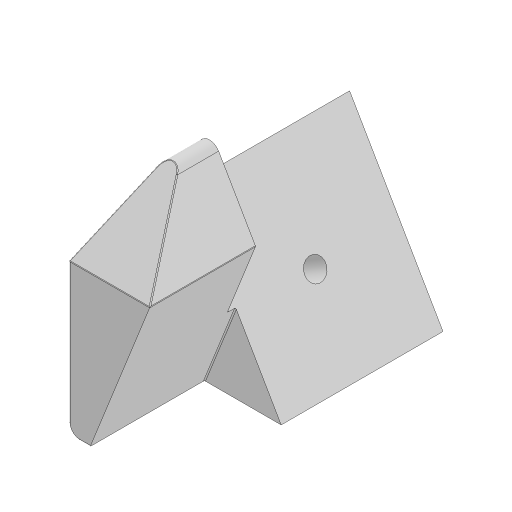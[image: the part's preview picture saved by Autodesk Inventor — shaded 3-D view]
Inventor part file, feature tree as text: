
AUTODESK INVENTOR PART (.ipt)
format: ipt  version: 2024.3 (Build 283343000, 343)  size: 207,872 bytes
history: native  units: mm
features: other x19, extrude x6, sketch x3, plane x2, fillet x2
ambient origin geometry x8: Origin, YZ Plane, XZ Plane, XY Plane, X Axis, Y Axis, Z Axis, Center Point
bodies: Body1 (feature_tree)
feature tree (32):
  sketch  "草圖1"
  extrude  "擠出3"  Depth=0.763247mm
  extrude  "擠出4"  Depth=0.25mm
  extrude  "擠出5"  Depth=21.008922mm
  plane  "工作平面5"
  extrude  "擠出6"  Depth=0.25mm
  sketch  "草圖3"
  plane  "工作平面6"
  extrude  "擠出7"  Depth=5.0mm
  extrude  "擠出8"  Depth=0.25mm
  fillet  "圓角1"  Radius=10.0mm
  fillet  "圓角2"  [1 undecoded]
  other  "直接編輯1"
  other  "參考1"
  other  "參考2"
  other  "參考3"
  other  "參考4"
  other  "參考5"
  other  "參考6"
  other  "參考7"
  other  "參考8"
  other  "參考9"
  other  "參考10"
  other  "參考11"
  sketch  "草圖2"
  other  "參考12"
  other  "參考13"
  other  "Atom_3_Lite_Upgrade.iam"
  other  "esun_ebox_holder_front:1"
  other  "Atom_3_lite:1"
  other  "eBox:1"
  other  "移動1"
note: 1 required parameter value undecoded (feature->parameter linkage not recoverable at this tier; creation-order binding heuristic only, values carry confidence <= 0.55)
